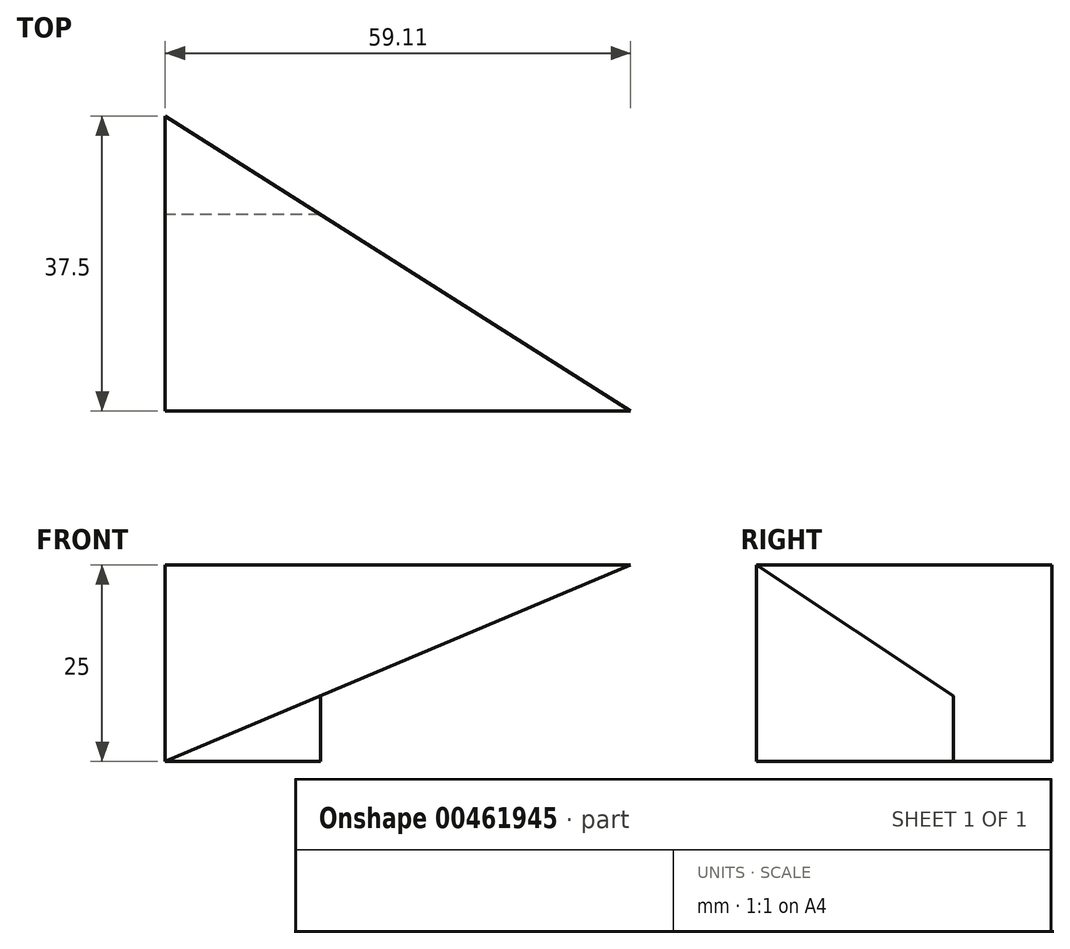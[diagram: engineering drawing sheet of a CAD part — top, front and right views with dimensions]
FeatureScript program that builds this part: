
annotation { "Feature Type Name" : "Feature", "Feature Type Description" : "" }
export const myFeature = defineFeature(function(context is Context, id is Id, definition is map)
    precondition{}
    {
        {
            var Q0;
            Q0=qCreatedBy(makeId("Top.planeOp"),FACE);
            var sketch = newSketch(context, id + "F0", { "sketchPlane" : qUnion([Q0])});
            skLineSegment(sketch, "E0", {"start": v(-118.59, 97.3) * mm, "end": v(-118.59, -52.7) * mm});
            skPoint(sketch, "E1", {"position": v(-118.59, 22.3) * mm});
            skLineSegment(sketch, "E2", {"start": v(-118.59, 59.8) * mm, "end": v(-59.48, 22.3) * mm});
            skLineSegment(sketch, "E3", {"start": v(-118.59, -52.7) * mm, "end": v(-59.48, 22.3) * mm});
            skLineSegment(sketch, "E4", {"start": v(-59.48, 22.3) * mm, "end": v(-118.59, 22.3) * mm});
            skSolve(sketch);
        }
        {
            var Q0;
            {var subQ0=sQuery(id+"F0.wireOp",EDGE,"E2");Q0=makeQuery(id+"F0.imprint","IMPRINT",FACE,{"disambiguationData":[TD([[makeQuery(id+"F0.imprint","IMPRINT",EDGE,{"derivedFrom":subQ0}),-1.0]])]});}
            extrude(context, id + "F1", {"entities" : qUnion([Q0]), "depth" : 25 * mm});
        }
        {
            var Q0;
            Q0=makeQuery(id+"F1.opExtrude","SWEPT_FACE",FACE,{"disambiguationData":[OSD([sQuery(id+"F0.wireOp",EDGE,"E4")])]});
            var sketch = newSketch(context, id + "F2", { "sketchPlane" : qUnion([Q0])});
            skLineSegment(sketch, "E5", {"start": v(-118.59, 0) * mm, "end": v(-59.48, 25) * mm});
            skSolve(sketch);
        }
        {
            var Q0;
            Q0=makeQuery(id+"F2.imprint","IMPRINT",FACE,{"disambiguationData":[TD([[makeQuery(id+"F2.imprint","IMPRINT",EDGE,{"derivedFrom":sQuery(id+"F2.wireOp",EDGE,"E5")}),-1.0]])]});
            extrude(context, id + "F3", {"entities" : qUnion([Q0]), "operationType" : NewBodyOperationType.REMOVE, "oppositeDirection" : true, "depth" : 25 * mm});
        }
    });
